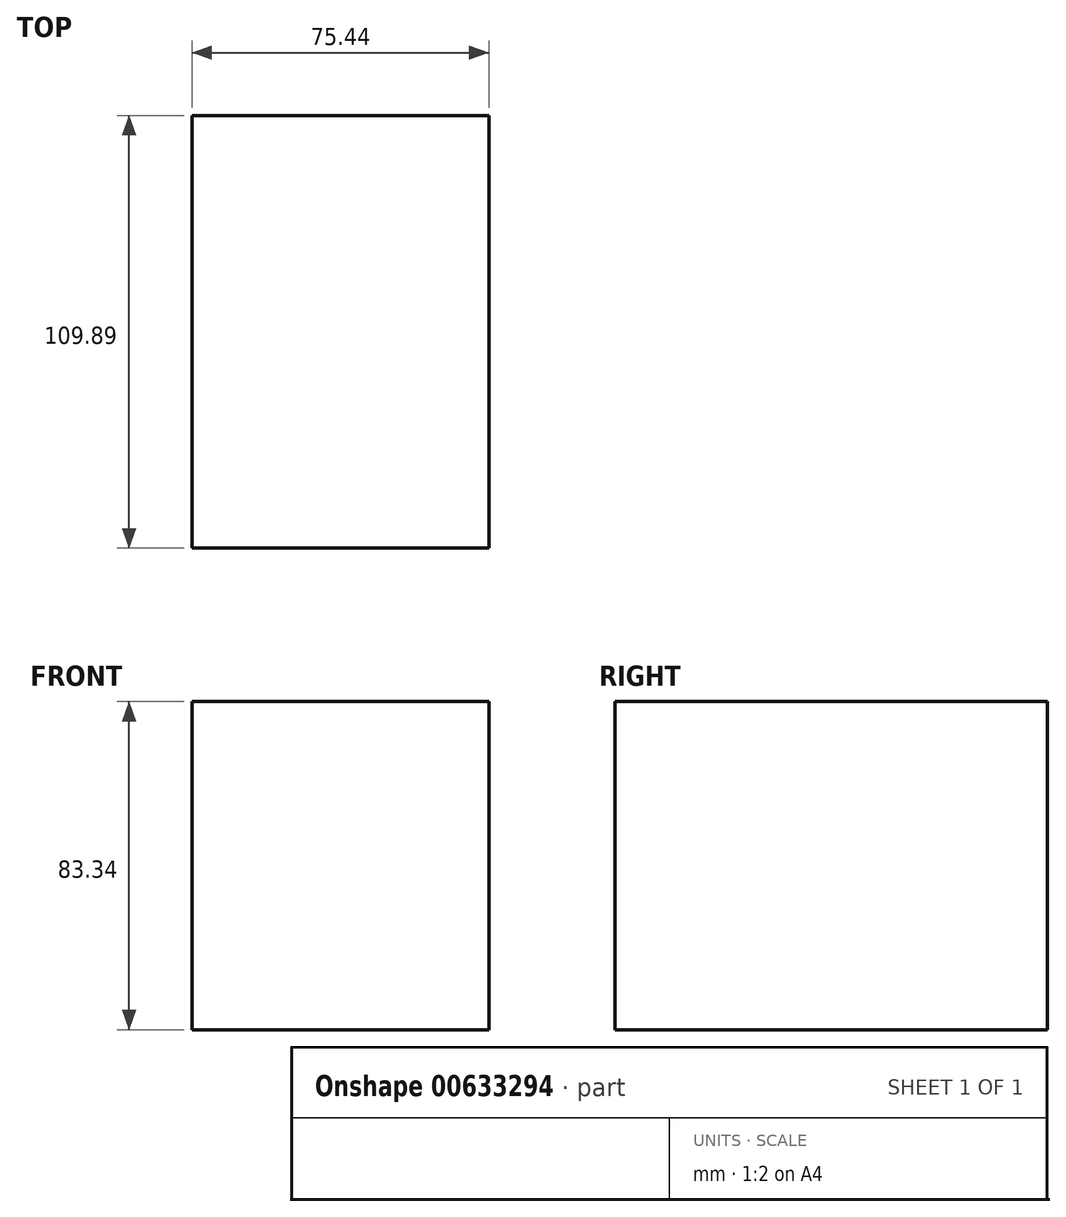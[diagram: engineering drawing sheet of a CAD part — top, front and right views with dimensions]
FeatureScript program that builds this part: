
annotation { "Feature Type Name" : "Feature", "Feature Type Description" : "" }
export const myFeature = defineFeature(function(context is Context, id is Id, definition is map)
    precondition{}
    {
        {
            var Q0;
            Q0=qCreatedBy(makeId("Right.planeOp"),FACE);
            var sketch = newSketch(context, id + "F0", { "sketchPlane" : qUnion([Q0])});
            skLineSegment(sketch, "E0.bottom", {"start": v(-46.92, 46.2) * mm, "end": v(62.97, 46.2) * mm});
            skLineSegment(sketch, "E0.top", {"start": v(-46.92, -37.14) * mm, "end": v(62.97, -37.14) * mm});
            skLineSegment(sketch, "E0.left", {"start": v(-46.92, 46.2) * mm, "end": v(-46.92, -37.14) * mm});
            skLineSegment(sketch, "E0.right", {"start": v(62.97, 46.2) * mm, "end": v(62.97, -37.14) * mm});
            skSolve(sketch);
        }
        {
            var Q0;
            Q0 = qSketchRegion(id + "F0", true);
            extrude(context, id + "F1", {"entities" : qUnion([Q0]), "depth" : 75.44 * mm, "offsetDistance" : 25.4 * mm});
        }
    });
